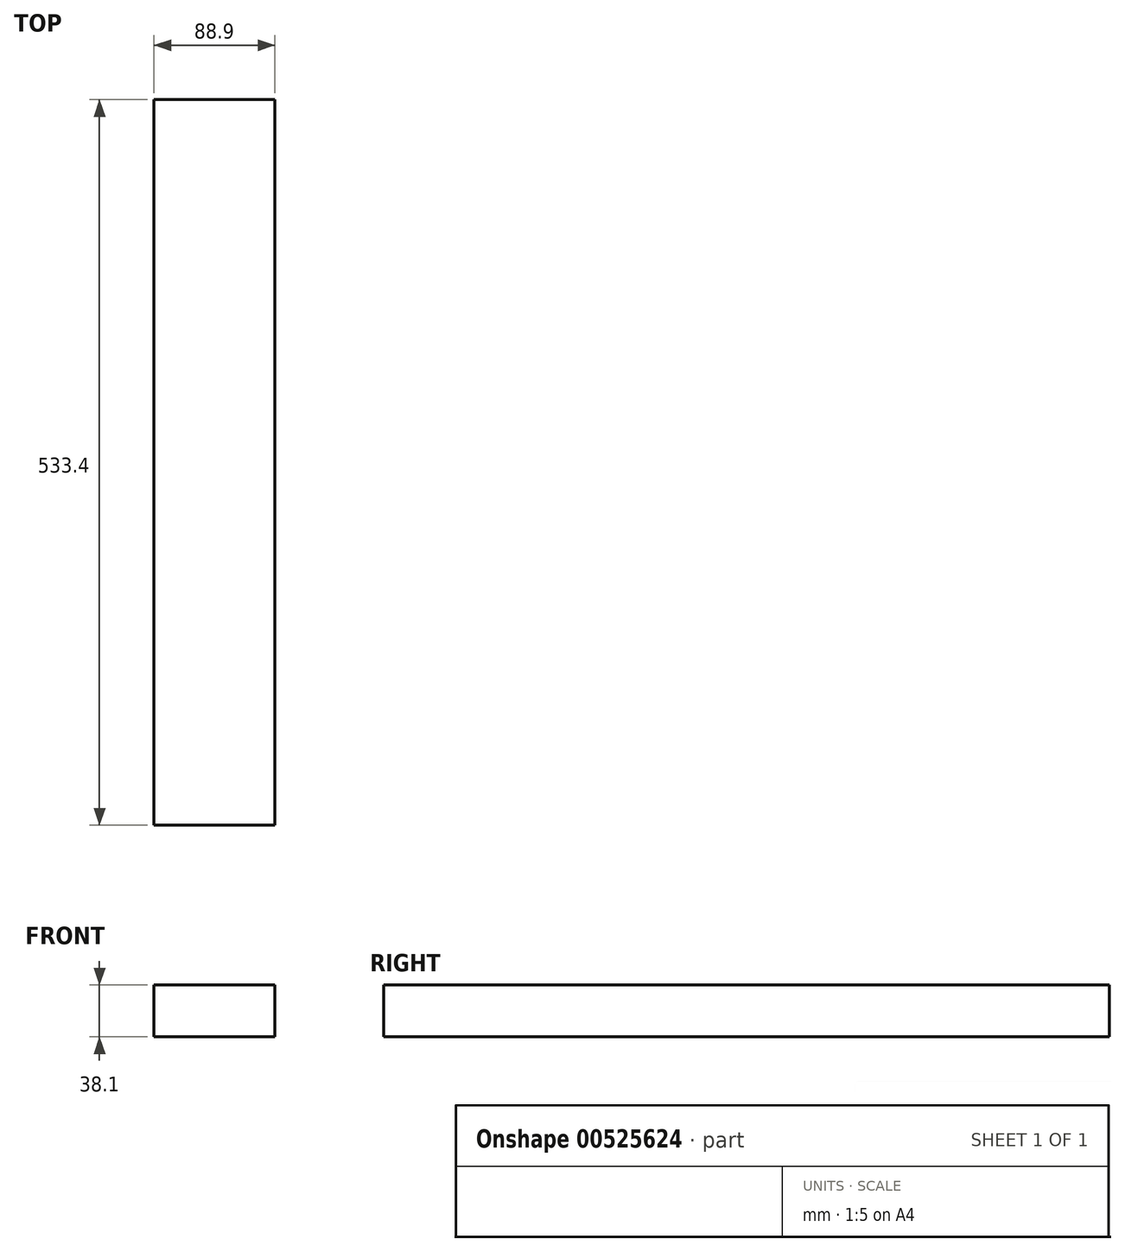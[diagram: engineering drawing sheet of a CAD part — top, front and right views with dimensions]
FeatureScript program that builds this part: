
annotation { "Feature Type Name" : "Feature", "Feature Type Description" : "" }
export const myFeature = defineFeature(function(context is Context, id is Id, definition is map)
    precondition{}
    {
        {
            var Q0;
            Q0=qCreatedBy(makeId("Front.planeOp"),FACE);
            var sketch = newSketch(context, id + "F0", { "sketchPlane" : qUnion([Q0])});
            skLineSegment(sketch, "E0.bottom", {"start": v(44.45, -19.05) * mm, "end": v(-44.45, -19.05) * mm});
            skLineSegment(sketch, "E0.top", {"start": v(44.45, 19.05) * mm, "end": v(-44.45, 19.05) * mm});
            skLineSegment(sketch, "E0.left", {"start": v(44.45, -19.05) * mm, "end": v(44.45, 19.05) * mm});
            skLineSegment(sketch, "E0.right", {"start": v(-44.45, -19.05) * mm, "end": v(-44.45, 19.05) * mm});
            skPoint(sketch, "E0.middle", {"position": v(0, 0) * mm});
            skSolve(sketch);
        }
        {
            var Q0;
            Q0 = qSketchRegion(id + "F0", true);
            extrude(context, id + "F1", {"entities" : qUnion([Q0]), "depth" : 533.4 * mm, "offsetDistance" : 25.4 * mm});
        }
    });
